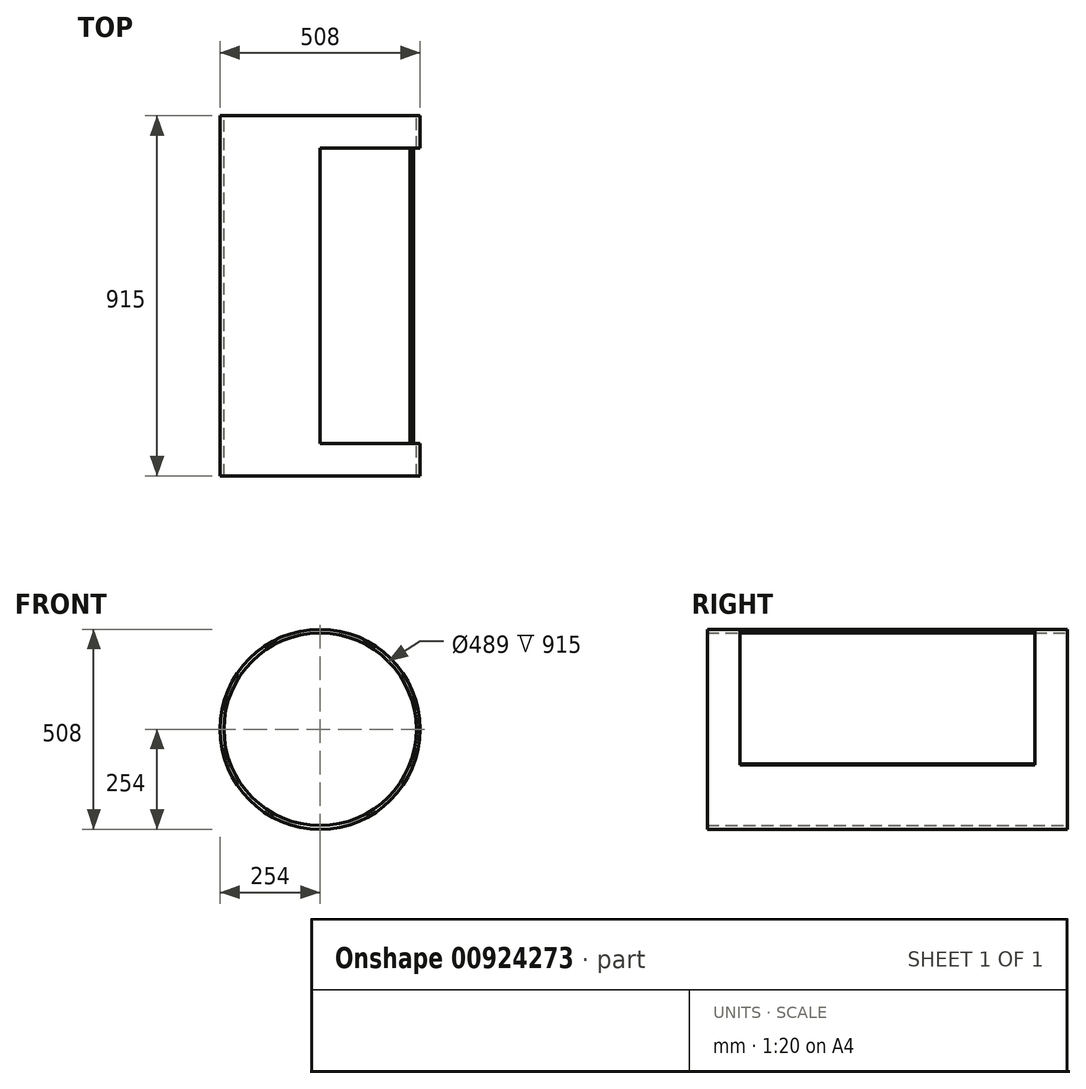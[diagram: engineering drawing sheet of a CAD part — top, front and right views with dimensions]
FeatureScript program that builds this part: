
annotation { "Feature Type Name" : "Feature", "Feature Type Description" : "" }
export const myFeature = defineFeature(function(context is Context, id is Id, definition is map)
    precondition{}
    {
        {
            var Q0;
            Q0=qCreatedBy(makeId("Front.planeOp"),FACE);
            var sketch = newSketch(context, id + "F0", { "sketchPlane" : qUnion([Q0])});
            skCircle(sketch, "E0", {"center": v(0, 0) * mm, "radius": 254 * mm});
            skCircle(sketch, "E1", {"center": v(0, 0) * mm, "radius": 244.5 * mm});
            skSolve(sketch);
        }
        {
            var Q0;
            Q0=makeQuery(id+"F0.imprint","IMPRINT",FACE,{"disambiguationData":[TD([[makeQuery(id+"F0.imprint","IMPRINT",EDGE,{"derivedFrom":sQuery(id+"F0.wireOp",EDGE,"E0")}),1.0]])]});
            extrude(context, id + "F1", {"entities" : qUnion([Q0]), "endBound" : BoundingType.SYMMETRIC, "depth" : 915 * mm, "offsetDistance" : 25.4 * mm});
        }
        {
            var Q0;
            Q0=qCreatedBy(makeId("Front.planeOp"),FACE);
            var sketch = newSketch(context, id + "F2", { "sketchPlane" : qUnion([Q0])});
            skArc(sketch, "E2", {"start": v(0, 254) * mm, "mid": v(209.33, 143.87) * mm, "end": v(237.13, -91.03) * mm});
            skLineSegment(sketch, "E3", {"start": v(0, 254) * mm, "end": v(0, 0) * mm});
            skLineSegment(sketch, "E4", {"start": v(0, 0) * mm, "end": v(237.13, -91.03) * mm});
            skArc(sketch, "E5", {"start": v(0, 244.5) * mm, "mid": v(201.5, 138.49) * mm, "end": v(228.26, -87.62) * mm});
            skLineSegment(sketch, "E6", {"start": v(228.26, -87.62) * mm, "end": v(237.13, -91.03) * mm});
            skLineSegment(sketch, "E7", {"start": v(0, 254) * mm, "end": v(0, 244.5) * mm});
            skSolve(sketch);
        }
        {
            var Q0;
            Q0=qSketchRegion(id+"F2",true);
            extrude(context, id + "F3", {"entities" : qUnion([Q0]), "operationType" : NewBodyOperationType.REMOVE, "endBound" : BoundingType.SYMMETRIC, "oppositeDirection" : true, "depth" : 750 * mm, "offsetDistance" : 25.4 * mm});
        }
    });
